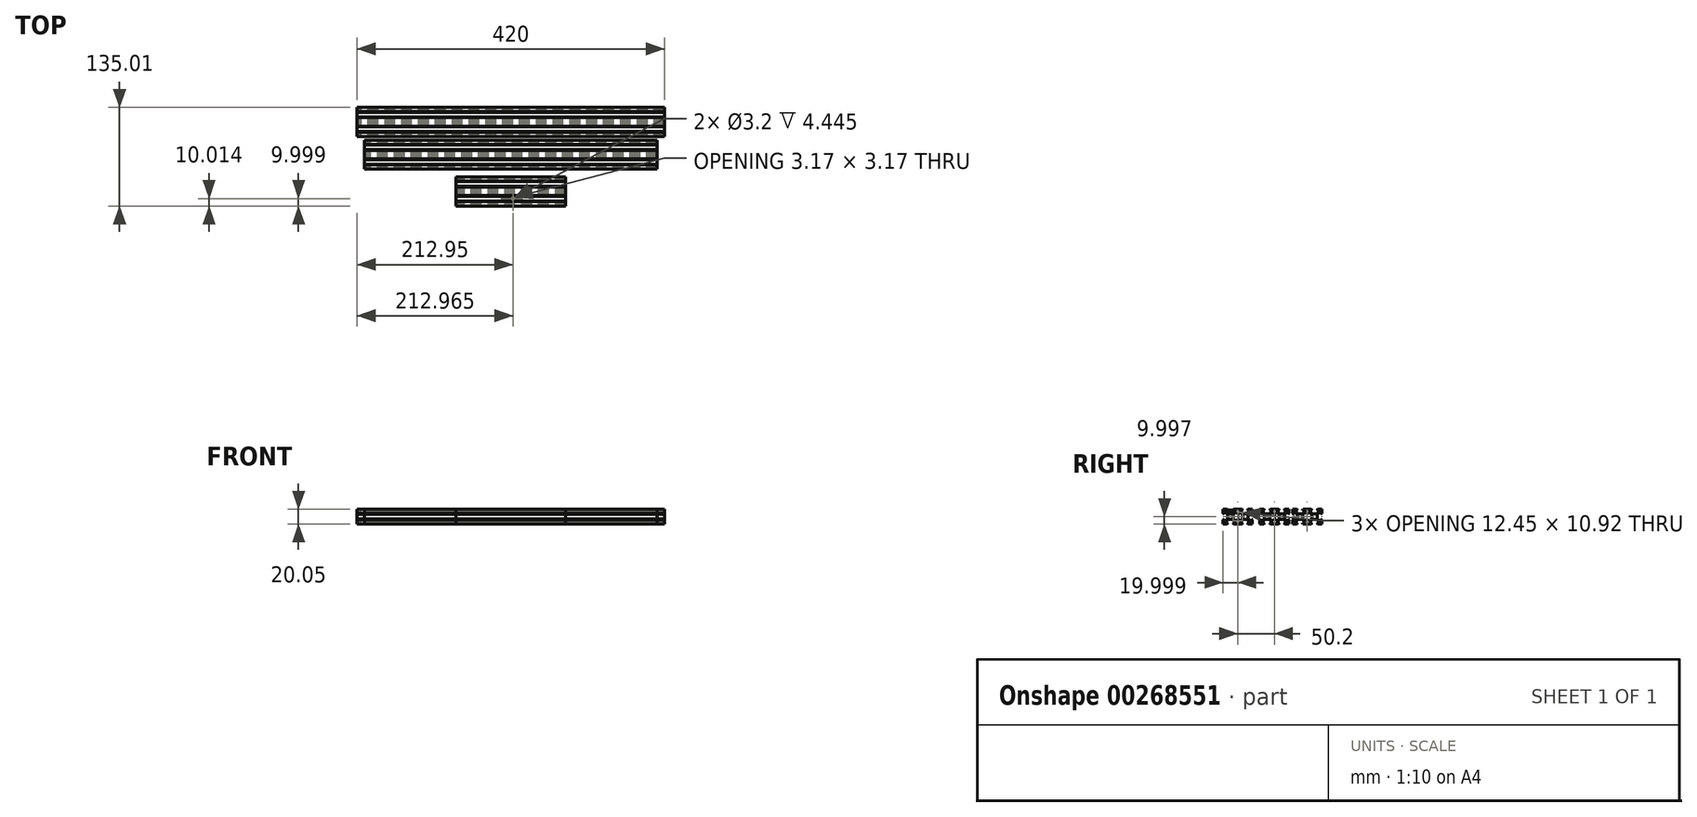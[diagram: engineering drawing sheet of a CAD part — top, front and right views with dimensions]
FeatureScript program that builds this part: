
annotation { "Feature Type Name" : "Feature", "Feature Type Description" : "" }
export const myFeature = defineFeature(function(context is Context, id is Id, definition is map)
    precondition{}
    {
        {
            var Q0;
            Q0=qCreatedBy(makeId("Right.planeOp"),FACE);
            var sketch = newSketch(context, id + "F0", { "sketchPlane" : qUnion([Q0])});
            skLineSegment(sketch, "E0.bottom", {"start": v(10.27, -9.71) * mm, "end": v(-9.73, -9.71) * mm});
            skLineSegment(sketch, "E0.top", {"start": v(10.27, 10.29) * mm, "end": v(-9.73, 10.29) * mm});
            skLineSegment(sketch, "E0.left", {"start": v(10.27, -9.71) * mm, "end": v(10.27, 10.29) * mm});
            skLineSegment(sketch, "E0.right", {"start": v(-9.73, -9.71) * mm, "end": v(-9.73, 10.29) * mm});
            skPoint(sketch, "E0.middle", {"position": v(0.27, 0.29) * mm});
            skLineSegment(sketch, "E1", {"start": v(4.51, 10.29) * mm, "end": v(3.38, 8.71) * mm});
            skLineSegment(sketch, "E2", {"start": v(3.38, 8.71) * mm, "end": v(3.38, 8.5) * mm});
            skLineSegment(sketch, "E3", {"start": v(3.38, 8.5) * mm, "end": v(5.73, 8.5) * mm});
            skLineSegment(sketch, "E4", {"start": v(5.73, 8.5) * mm, "end": v(5.73, 6.73) * mm});
            skLineSegment(sketch, "E5", {"start": v(5.73, 6.73) * mm, "end": v(3.38, 4.06) * mm});
            skLineSegment(sketch, "E6", {"start": v(3.38, 4.06) * mm, "end": v(0.27, 4.06) * mm});
            skLineSegment(sketch, "E7", {"start": v(0.27, 16.16) * mm, "end": v(0.27, -18.08) * mm, "construction": true});
            skPoint(sketch, "E7.endSnap0", {"position": v(0.27, -9.71) * mm});
            skLineSegment(sketch, "E8.0", {"start": v(5.73, 16.16) * mm, "end": v(5.73, -18.08) * mm, "construction": true});
            skLineSegment(sketch, "E9.MirrorCS", {"start": v(-3.98, 10.29) * mm, "end": v(-2.84, 8.71) * mm});
            skLineSegment(sketch, "E10.MirrorCS", {"start": v(-2.84, 8.71) * mm, "end": v(-2.84, 8.5) * mm});
            skLineSegment(sketch, "E11.MirrorCS", {"start": v(-2.84, 8.5) * mm, "end": v(-5.2, 8.5) * mm});
            skLineSegment(sketch, "E12.MirrorCS", {"start": v(-5.2, 16.16) * mm, "end": v(-5.2, -18.08) * mm, "construction": true});
            skLineSegment(sketch, "E13.MirrorCS", {"start": v(-5.2, 6.73) * mm, "end": v(-2.84, 4.06) * mm});
            skLineSegment(sketch, "E14.MirrorCS", {"start": v(-2.84, 4.06) * mm, "end": v(0.27, 4.06) * mm});
            skLineSegment(sketch, "E15.MirrorCS", {"start": v(-5.2, 8.5) * mm, "end": v(-5.2, 6.73) * mm});
            skLineSegment(sketch, "E16.1.0", {"start": v(-3.5, 3.4) * mm, "end": v(-3.5, 0.29) * mm});
            skLineSegment(sketch, "E16.1.1", {"start": v(-3.5, -2.82) * mm, "end": v(-3.5, 0.29) * mm});
            skLineSegment(sketch, "E16.1.2", {"start": v(-6.18, -5.17) * mm, "end": v(-3.5, -2.82) * mm});
            skLineSegment(sketch, "E16.1.3", {"start": v(-7.95, 3.4) * mm, "end": v(-7.95, 5.75) * mm});
            skLineSegment(sketch, "E16.1.4", {"start": v(-9.73, 4.53) * mm, "end": v(-8.16, 3.4) * mm});
            skLineSegment(sketch, "E16.1.5", {"start": v(-7.95, 5.75) * mm, "end": v(-6.18, 5.75) * mm});
            skLineSegment(sketch, "E16.1.6", {"start": v(-9.73, -3.96) * mm, "end": v(-8.16, -2.82) * mm});
            skLineSegment(sketch, "E16.1.7", {"start": v(-6.18, 5.75) * mm, "end": v(-3.5, 3.4) * mm});
            skLineSegment(sketch, "E16.1.8", {"start": v(-7.95, -5.17) * mm, "end": v(-6.18, -5.17) * mm});
            skLineSegment(sketch, "E16.1.9", {"start": v(-7.95, -2.82) * mm, "end": v(-7.95, -5.17) * mm});
            skLineSegment(sketch, "E16.1.10", {"start": v(-8.16, -2.82) * mm, "end": v(-7.95, -2.82) * mm});
            skLineSegment(sketch, "E16.1.11", {"start": v(-8.16, 3.4) * mm, "end": v(-7.95, 3.4) * mm});
            skLineSegment(sketch, "E16.2.0", {"start": v(-2.84, -3.5) * mm, "end": v(0.27, -3.5) * mm});
            skLineSegment(sketch, "E16.2.1", {"start": v(3.38, -3.5) * mm, "end": v(0.27, -3.5) * mm});
            skLineSegment(sketch, "E16.2.2", {"start": v(5.73, -6.16) * mm, "end": v(3.38, -3.5) * mm});
            skLineSegment(sketch, "E16.2.3", {"start": v(-2.84, -7.94) * mm, "end": v(-5.2, -7.94) * mm});
            skLineSegment(sketch, "E16.2.4", {"start": v(-3.98, -9.71) * mm, "end": v(-2.84, -8.14) * mm});
            skLineSegment(sketch, "E16.2.5", {"start": v(-5.2, -7.94) * mm, "end": v(-5.2, -6.16) * mm});
            skLineSegment(sketch, "E16.2.6", {"start": v(4.51, -9.71) * mm, "end": v(3.38, -8.14) * mm});
            skLineSegment(sketch, "E16.2.7", {"start": v(-5.2, -6.16) * mm, "end": v(-2.84, -3.5) * mm});
            skLineSegment(sketch, "E16.2.8", {"start": v(5.73, -7.94) * mm, "end": v(5.73, -6.16) * mm});
            skLineSegment(sketch, "E16.2.9", {"start": v(3.38, -7.94) * mm, "end": v(5.73, -7.94) * mm});
            skLineSegment(sketch, "E16.2.10", {"start": v(3.38, -8.14) * mm, "end": v(3.38, -7.94) * mm});
            skLineSegment(sketch, "E16.2.11", {"start": v(-2.84, -8.14) * mm, "end": v(-2.84, -7.94) * mm});
            skLineSegment(sketch, "E16.3.0", {"start": v(4.05, -2.82) * mm, "end": v(4.05, 0.29) * mm});
            skLineSegment(sketch, "E16.3.1", {"start": v(4.05, 3.4) * mm, "end": v(4.05, 0.29) * mm});
            skLineSegment(sketch, "E16.3.2", {"start": v(6.71, 5.75) * mm, "end": v(4.05, 3.4) * mm});
            skLineSegment(sketch, "E16.3.3", {"start": v(8.5, -2.82) * mm, "end": v(8.5, -5.17) * mm});
            skLineSegment(sketch, "E16.3.4", {"start": v(10.27, -3.96) * mm, "end": v(8.7, -2.82) * mm});
            skLineSegment(sketch, "E16.3.5", {"start": v(8.5, -5.17) * mm, "end": v(6.71, -5.17) * mm});
            skLineSegment(sketch, "E16.3.6", {"start": v(10.27, 4.53) * mm, "end": v(8.7, 3.4) * mm});
            skLineSegment(sketch, "E16.3.7", {"start": v(6.71, -5.17) * mm, "end": v(4.05, -2.82) * mm});
            skLineSegment(sketch, "E16.3.8", {"start": v(8.5, 5.75) * mm, "end": v(6.71, 5.75) * mm});
            skLineSegment(sketch, "E16.3.9", {"start": v(8.5, 3.4) * mm, "end": v(8.5, 5.75) * mm});
            skLineSegment(sketch, "E16.3.10", {"start": v(8.7, 3.4) * mm, "end": v(8.5, 3.4) * mm});
            skLineSegment(sketch, "E16.3.11", {"start": v(8.7, -2.82) * mm, "end": v(8.5, -2.82) * mm});
            skLineSegment(sketch, "E17.bottom", {"start": v(30.27, -9.71) * mm, "end": v(10.27, -9.71) * mm});
            skLineSegment(sketch, "E17.top", {"start": v(30.27, 10.29) * mm, "end": v(10.27, 10.29) * mm});
            skLineSegment(sketch, "E17.left", {"start": v(30.27, -9.71) * mm, "end": v(30.27, 10.29) * mm});
            skPoint(sketch, "E17.middle", {"position": v(20.27, 0.29) * mm});
            skLineSegment(sketch, "E18", {"start": v(24.51, 10.29) * mm, "end": v(23.38, 8.71) * mm});
            skLineSegment(sketch, "E19", {"start": v(23.38, 8.71) * mm, "end": v(23.38, 8.5) * mm});
            skLineSegment(sketch, "E20", {"start": v(23.38, 8.5) * mm, "end": v(25.73, 8.5) * mm});
            skLineSegment(sketch, "E21", {"start": v(25.73, 8.5) * mm, "end": v(25.73, 6.73) * mm});
            skLineSegment(sketch, "E22", {"start": v(25.73, 6.73) * mm, "end": v(23.38, 4.06) * mm});
            skLineSegment(sketch, "E23", {"start": v(23.38, 4.06) * mm, "end": v(20.27, 4.06) * mm});
            skPoint(sketch, "E24.endSnap0", {"position": v(20.27, -9.71) * mm});
            skLineSegment(sketch, "E25.MirrorCS", {"start": v(16.02, 10.29) * mm, "end": v(17.16, 8.71) * mm});
            skLineSegment(sketch, "E26.MirrorCS", {"start": v(17.16, 8.71) * mm, "end": v(17.16, 8.5) * mm});
            skLineSegment(sketch, "E27.MirrorCS", {"start": v(17.16, 8.5) * mm, "end": v(14.8, 8.5) * mm});
            skLineSegment(sketch, "E28.MirrorCS", {"start": v(14.8, 6.73) * mm, "end": v(17.16, 4.06) * mm});
            skLineSegment(sketch, "E29.MirrorCS", {"start": v(17.16, 4.06) * mm, "end": v(20.27, 4.06) * mm});
            skLineSegment(sketch, "E30.MirrorCS", {"start": v(14.8, 8.5) * mm, "end": v(14.8, 6.73) * mm});
            skLineSegment(sketch, "E31.1.0", {"start": v(16.5, 3.4) * mm, "end": v(16.5, 0.29) * mm});
            skLineSegment(sketch, "E31.1.1", {"start": v(16.5, -2.82) * mm, "end": v(16.5, 0.29) * mm});
            skLineSegment(sketch, "E31.1.2", {"start": v(13.82, -5.17) * mm, "end": v(16.5, -2.82) * mm});
            skLineSegment(sketch, "E31.1.3", {"start": v(12.05, 3.4) * mm, "end": v(12.05, 5.75) * mm});
            skLineSegment(sketch, "E31.1.4", {"start": v(10.27, 4.53) * mm, "end": v(11.84, 3.4) * mm});
            skLineSegment(sketch, "E31.1.5", {"start": v(12.05, 5.75) * mm, "end": v(13.82, 5.75) * mm});
            skLineSegment(sketch, "E31.1.6", {"start": v(10.27, -3.96) * mm, "end": v(11.84, -2.82) * mm});
            skLineSegment(sketch, "E31.1.7", {"start": v(13.82, 5.75) * mm, "end": v(16.5, 3.4) * mm});
            skLineSegment(sketch, "E31.1.8", {"start": v(12.05, -5.17) * mm, "end": v(13.82, -5.17) * mm});
            skLineSegment(sketch, "E31.1.9", {"start": v(12.05, -2.82) * mm, "end": v(12.05, -5.17) * mm});
            skLineSegment(sketch, "E31.1.10", {"start": v(11.84, -2.82) * mm, "end": v(12.05, -2.82) * mm});
            skLineSegment(sketch, "E31.1.11", {"start": v(11.84, 3.4) * mm, "end": v(12.05, 3.4) * mm});
            skLineSegment(sketch, "E31.2.0", {"start": v(17.16, -3.5) * mm, "end": v(20.27, -3.5) * mm});
            skLineSegment(sketch, "E31.2.1", {"start": v(23.38, -3.5) * mm, "end": v(20.27, -3.5) * mm});
            skLineSegment(sketch, "E31.2.2", {"start": v(25.73, -6.16) * mm, "end": v(23.38, -3.5) * mm});
            skLineSegment(sketch, "E31.2.3", {"start": v(17.16, -7.94) * mm, "end": v(14.8, -7.94) * mm});
            skLineSegment(sketch, "E31.2.4", {"start": v(16.02, -9.71) * mm, "end": v(17.16, -8.14) * mm});
            skLineSegment(sketch, "E31.2.5", {"start": v(14.8, -7.94) * mm, "end": v(14.8, -6.16) * mm});
            skLineSegment(sketch, "E31.2.6", {"start": v(24.51, -9.71) * mm, "end": v(23.38, -8.14) * mm});
            skLineSegment(sketch, "E31.2.7", {"start": v(14.8, -6.16) * mm, "end": v(17.16, -3.5) * mm});
            skLineSegment(sketch, "E31.2.8", {"start": v(25.73, -7.94) * mm, "end": v(25.73, -6.16) * mm});
            skLineSegment(sketch, "E31.2.9", {"start": v(23.38, -7.94) * mm, "end": v(25.73, -7.94) * mm});
            skLineSegment(sketch, "E31.2.10", {"start": v(23.38, -8.14) * mm, "end": v(23.38, -7.94) * mm});
            skLineSegment(sketch, "E31.2.11", {"start": v(17.16, -8.14) * mm, "end": v(17.16, -7.94) * mm});
            skLineSegment(sketch, "E31.3.0", {"start": v(24.05, -2.82) * mm, "end": v(24.05, 0.29) * mm});
            skLineSegment(sketch, "E31.3.1", {"start": v(24.05, 3.4) * mm, "end": v(24.05, 0.29) * mm});
            skLineSegment(sketch, "E31.3.2", {"start": v(26.71, 5.75) * mm, "end": v(24.05, 3.4) * mm});
            skLineSegment(sketch, "E31.3.3", {"start": v(28.5, -2.82) * mm, "end": v(28.5, -5.17) * mm});
            skLineSegment(sketch, "E31.3.4", {"start": v(30.27, -3.96) * mm, "end": v(28.7, -2.82) * mm});
            skLineSegment(sketch, "E31.3.5", {"start": v(28.5, -5.17) * mm, "end": v(26.71, -5.17) * mm});
            skLineSegment(sketch, "E31.3.6", {"start": v(30.27, 4.53) * mm, "end": v(28.7, 3.4) * mm});
            skLineSegment(sketch, "E31.3.7", {"start": v(26.71, -5.17) * mm, "end": v(24.05, -2.82) * mm});
            skLineSegment(sketch, "E31.3.8", {"start": v(28.5, 5.75) * mm, "end": v(26.71, 5.75) * mm});
            skLineSegment(sketch, "E31.3.9", {"start": v(28.5, 3.4) * mm, "end": v(28.5, 5.75) * mm});
            skLineSegment(sketch, "E31.3.10", {"start": v(28.7, 3.4) * mm, "end": v(28.5, 3.4) * mm});
            skLineSegment(sketch, "E31.3.11", {"start": v(28.7, -2.82) * mm, "end": v(28.5, -2.82) * mm});
            skSolve(sketch);
        }
        {
            var Q0;
            {var subQ11=sQuery(id+"F0.wireOp",EDGE,"E18");Q0=makeQuery(id+"F0.imprint","IMPRINT",FACE,{"disambiguationData":[TD([[makeQuery(id+"F0.imprint","IMPRINT",EDGE,{"derivedFrom":subQ11}),1.0]])]});}
            var Q1;
            {var subQ12=sQuery(id+"F0.wireOp",EDGE,"E1");Q1=makeQuery(id+"F0.imprint","IMPRINT",FACE,{"disambiguationData":[TD([[makeQuery(id+"F0.imprint","IMPRINT",EDGE,{"derivedFrom":subQ12}),1.0]])]});}
            extrude(context, id + "F1", {"entities" : qUnion([Q0, Q1]), "endBound" : BoundingType.SYMMETRIC, "depth" : 420 * mm});
        }
        {
            var Q0;
            Q0=qCreatedBy(makeId("Right.planeOp"),FACE);
            var sketch = newSketch(context, id + "F2", { "sketchPlane" : qUnion([Q0])});
            skLineSegment(sketch, "E32.bottom", {"start": v(0.66, -9.76) * mm, "end": v(-19.34, -9.76) * mm});
            skLineSegment(sketch, "E32.top", {"start": v(0.66, 10.24) * mm, "end": v(-19.34, 10.24) * mm});
            skLineSegment(sketch, "E32.left", {"start": v(0.66, -9.76) * mm, "end": v(0.66, 10.24) * mm});
            skLineSegment(sketch, "E32.right", {"start": v(-19.34, -9.76) * mm, "end": v(-19.34, 10.24) * mm});
            skPoint(sketch, "E32.middle", {"position": v(-9.34, 0.24) * mm});
            skLineSegment(sketch, "E33", {"start": v(-5.1, 10.24) * mm, "end": v(-6.23, 8.66) * mm});
            skLineSegment(sketch, "E34", {"start": v(-6.23, 8.66) * mm, "end": v(-6.23, 8.46) * mm});
            skLineSegment(sketch, "E35", {"start": v(-6.23, 8.46) * mm, "end": v(-3.88, 8.46) * mm});
            skLineSegment(sketch, "E36", {"start": v(-3.88, 8.46) * mm, "end": v(-3.88, 6.68) * mm});
            skLineSegment(sketch, "E37", {"start": v(-3.88, 6.68) * mm, "end": v(-6.23, 4.01) * mm});
            skLineSegment(sketch, "E38", {"start": v(-6.23, 4.01) * mm, "end": v(-9.34, 4.01) * mm});
            skLineSegment(sketch, "E39", {"start": v(-9.34, 16.11) * mm, "end": v(-9.34, -18.13) * mm, "construction": true});
            skPoint(sketch, "E39.endSnap0", {"position": v(-9.34, -9.76) * mm});
            skLineSegment(sketch, "E40.0", {"start": v(-3.88, 16.11) * mm, "end": v(-3.88, -18.13) * mm, "construction": true});
            skLineSegment(sketch, "E41.MirrorCS", {"start": v(-13.59, 10.24) * mm, "end": v(-12.45, 8.66) * mm});
            skLineSegment(sketch, "E42.MirrorCS", {"start": v(-12.45, 8.66) * mm, "end": v(-12.45, 8.46) * mm});
            skLineSegment(sketch, "E43.MirrorCS", {"start": v(-12.45, 8.46) * mm, "end": v(-14.8, 8.46) * mm});
            skLineSegment(sketch, "E44.MirrorCS", {"start": v(-14.8, 16.11) * mm, "end": v(-14.8, -18.13) * mm, "construction": true});
            skLineSegment(sketch, "E45.MirrorCS", {"start": v(-14.8, 6.68) * mm, "end": v(-12.45, 4.01) * mm});
            skLineSegment(sketch, "E46.MirrorCS", {"start": v(-12.45, 4.01) * mm, "end": v(-9.34, 4.01) * mm});
            skLineSegment(sketch, "E47.MirrorCS", {"start": v(-14.8, 8.46) * mm, "end": v(-14.8, 6.68) * mm});
            skLineSegment(sketch, "E48.1.0", {"start": v(-13.12, 3.35) * mm, "end": v(-13.12, 0.24) * mm});
            skLineSegment(sketch, "E48.1.1", {"start": v(-13.12, -2.87) * mm, "end": v(-13.12, 0.24) * mm});
            skLineSegment(sketch, "E48.1.2", {"start": v(-15.79, -5.22) * mm, "end": v(-13.12, -2.87) * mm});
            skLineSegment(sketch, "E48.1.3", {"start": v(-17.56, 3.35) * mm, "end": v(-17.56, 5.7) * mm});
            skLineSegment(sketch, "E48.1.4", {"start": v(-19.34, 4.48) * mm, "end": v(-17.77, 3.35) * mm});
            skLineSegment(sketch, "E48.1.5", {"start": v(-17.56, 5.7) * mm, "end": v(-15.79, 5.7) * mm});
            skLineSegment(sketch, "E48.1.6", {"start": v(-19.34, -4) * mm, "end": v(-17.77, -2.87) * mm});
            skLineSegment(sketch, "E48.1.7", {"start": v(-15.79, 5.7) * mm, "end": v(-13.12, 3.35) * mm});
            skLineSegment(sketch, "E48.1.8", {"start": v(-17.56, -5.22) * mm, "end": v(-15.79, -5.22) * mm});
            skLineSegment(sketch, "E48.1.9", {"start": v(-17.56, -2.87) * mm, "end": v(-17.56, -5.22) * mm});
            skLineSegment(sketch, "E48.1.10", {"start": v(-17.77, -2.87) * mm, "end": v(-17.56, -2.87) * mm});
            skLineSegment(sketch, "E48.1.11", {"start": v(-17.77, 3.35) * mm, "end": v(-17.56, 3.35) * mm});
            skLineSegment(sketch, "E48.2.0", {"start": v(-12.45, -3.54) * mm, "end": v(-9.34, -3.54) * mm});
            skLineSegment(sketch, "E48.2.1", {"start": v(-6.23, -3.54) * mm, "end": v(-9.34, -3.54) * mm});
            skLineSegment(sketch, "E48.2.2", {"start": v(-3.88, -6.2) * mm, "end": v(-6.23, -3.54) * mm});
            skLineSegment(sketch, "E48.2.3", {"start": v(-12.45, -7.98) * mm, "end": v(-14.8, -7.98) * mm});
            skLineSegment(sketch, "E48.2.4", {"start": v(-13.59, -9.76) * mm, "end": v(-12.45, -8.19) * mm});
            skLineSegment(sketch, "E48.2.5", {"start": v(-14.8, -7.98) * mm, "end": v(-14.8, -6.2) * mm});
            skLineSegment(sketch, "E48.2.6", {"start": v(-5.1, -9.76) * mm, "end": v(-6.23, -8.19) * mm});
            skLineSegment(sketch, "E48.2.7", {"start": v(-14.8, -6.2) * mm, "end": v(-12.45, -3.54) * mm});
            skLineSegment(sketch, "E48.2.8", {"start": v(-3.88, -7.98) * mm, "end": v(-3.88, -6.2) * mm});
            skLineSegment(sketch, "E48.2.9", {"start": v(-6.23, -7.98) * mm, "end": v(-3.88, -7.98) * mm});
            skLineSegment(sketch, "E48.2.10", {"start": v(-6.23, -8.19) * mm, "end": v(-6.23, -7.98) * mm});
            skLineSegment(sketch, "E48.2.11", {"start": v(-12.45, -8.19) * mm, "end": v(-12.45, -7.98) * mm});
            skLineSegment(sketch, "E48.3.0", {"start": v(-5.56, -2.87) * mm, "end": v(-5.56, 0.24) * mm});
            skLineSegment(sketch, "E48.3.1", {"start": v(-5.56, 3.35) * mm, "end": v(-5.56, 0.24) * mm});
            skLineSegment(sketch, "E48.3.2", {"start": v(-2.9, 5.7) * mm, "end": v(-5.56, 3.35) * mm});
            skLineSegment(sketch, "E48.3.3", {"start": v(-1.12, -2.87) * mm, "end": v(-1.12, -5.22) * mm});
            skLineSegment(sketch, "E48.3.4", {"start": v(0.66, -4) * mm, "end": v(-0.92, -2.87) * mm});
            skLineSegment(sketch, "E48.3.5", {"start": v(-1.12, -5.22) * mm, "end": v(-2.9, -5.22) * mm});
            skLineSegment(sketch, "E48.3.6", {"start": v(0.66, 4.48) * mm, "end": v(-0.92, 3.35) * mm});
            skLineSegment(sketch, "E48.3.7", {"start": v(-2.9, -5.22) * mm, "end": v(-5.56, -2.87) * mm});
            skLineSegment(sketch, "E48.3.8", {"start": v(-1.12, 5.7) * mm, "end": v(-2.9, 5.7) * mm});
            skLineSegment(sketch, "E48.3.9", {"start": v(-1.12, 3.35) * mm, "end": v(-1.12, 5.7) * mm});
            skLineSegment(sketch, "E48.3.10", {"start": v(-0.92, 3.35) * mm, "end": v(-1.12, 3.35) * mm});
            skLineSegment(sketch, "E48.3.11", {"start": v(-0.92, -2.87) * mm, "end": v(-1.12, -2.87) * mm});
            skLineSegment(sketch, "E49.bottom", {"start": v(20.66, -9.76) * mm, "end": v(0.66, -9.76) * mm});
            skLineSegment(sketch, "E49.top", {"start": v(20.66, 10.24) * mm, "end": v(0.66, 10.24) * mm});
            skLineSegment(sketch, "E49.left", {"start": v(20.66, -9.76) * mm, "end": v(20.66, 10.24) * mm});
            skPoint(sketch, "E49.middle", {"position": v(10.66, 0.24) * mm});
            skLineSegment(sketch, "E50", {"start": v(14.9, 10.24) * mm, "end": v(13.77, 8.66) * mm});
            skLineSegment(sketch, "E51", {"start": v(13.77, 8.66) * mm, "end": v(13.77, 8.46) * mm});
            skLineSegment(sketch, "E52", {"start": v(13.77, 8.46) * mm, "end": v(16.12, 8.46) * mm});
            skLineSegment(sketch, "E53", {"start": v(16.12, 8.46) * mm, "end": v(16.12, 6.68) * mm});
            skLineSegment(sketch, "E54", {"start": v(16.12, 6.68) * mm, "end": v(13.77, 4.01) * mm});
            skLineSegment(sketch, "E55", {"start": v(13.77, 4.01) * mm, "end": v(10.66, 4.01) * mm});
            skPoint(sketch, "E56.endSnap0", {"position": v(10.66, -9.76) * mm});
            skLineSegment(sketch, "E57.MirrorCS", {"start": v(6.41, 10.24) * mm, "end": v(7.55, 8.66) * mm});
            skLineSegment(sketch, "E58.MirrorCS", {"start": v(7.55, 8.66) * mm, "end": v(7.55, 8.46) * mm});
            skLineSegment(sketch, "E59.MirrorCS", {"start": v(7.55, 8.46) * mm, "end": v(5.2, 8.46) * mm});
            skLineSegment(sketch, "E60.MirrorCS", {"start": v(5.2, 6.68) * mm, "end": v(7.55, 4.01) * mm});
            skLineSegment(sketch, "E61.MirrorCS", {"start": v(7.55, 4.01) * mm, "end": v(10.66, 4.01) * mm});
            skLineSegment(sketch, "E62.MirrorCS", {"start": v(5.2, 8.46) * mm, "end": v(5.2, 6.68) * mm});
            skLineSegment(sketch, "E63.1.0", {"start": v(6.88, 3.35) * mm, "end": v(6.88, 0.24) * mm});
            skLineSegment(sketch, "E63.1.1", {"start": v(6.88, -2.87) * mm, "end": v(6.88, 0.24) * mm});
            skLineSegment(sketch, "E63.1.2", {"start": v(4.21, -5.22) * mm, "end": v(6.88, -2.87) * mm});
            skLineSegment(sketch, "E63.1.3", {"start": v(2.44, 3.35) * mm, "end": v(2.44, 5.7) * mm});
            skLineSegment(sketch, "E63.1.4", {"start": v(0.66, 4.48) * mm, "end": v(2.23, 3.35) * mm});
            skLineSegment(sketch, "E63.1.5", {"start": v(2.44, 5.7) * mm, "end": v(4.21, 5.7) * mm});
            skLineSegment(sketch, "E63.1.6", {"start": v(0.66, -4) * mm, "end": v(2.23, -2.87) * mm});
            skLineSegment(sketch, "E63.1.7", {"start": v(4.21, 5.7) * mm, "end": v(6.88, 3.35) * mm});
            skLineSegment(sketch, "E63.1.8", {"start": v(2.44, -5.22) * mm, "end": v(4.21, -5.22) * mm});
            skLineSegment(sketch, "E63.1.9", {"start": v(2.44, -2.87) * mm, "end": v(2.44, -5.22) * mm});
            skLineSegment(sketch, "E63.1.10", {"start": v(2.23, -2.87) * mm, "end": v(2.44, -2.87) * mm});
            skLineSegment(sketch, "E63.1.11", {"start": v(2.23, 3.35) * mm, "end": v(2.44, 3.35) * mm});
            skLineSegment(sketch, "E63.2.0", {"start": v(7.55, -3.54) * mm, "end": v(10.66, -3.54) * mm});
            skLineSegment(sketch, "E63.2.1", {"start": v(13.77, -3.54) * mm, "end": v(10.66, -3.54) * mm});
            skLineSegment(sketch, "E63.2.2", {"start": v(16.12, -6.2) * mm, "end": v(13.77, -3.54) * mm});
            skLineSegment(sketch, "E63.2.3", {"start": v(7.55, -7.98) * mm, "end": v(5.2, -7.98) * mm});
            skLineSegment(sketch, "E63.2.4", {"start": v(6.41, -9.76) * mm, "end": v(7.55, -8.19) * mm});
            skLineSegment(sketch, "E63.2.5", {"start": v(5.2, -7.98) * mm, "end": v(5.2, -6.2) * mm});
            skLineSegment(sketch, "E63.2.6", {"start": v(14.9, -9.76) * mm, "end": v(13.77, -8.19) * mm});
            skLineSegment(sketch, "E63.2.7", {"start": v(5.2, -6.2) * mm, "end": v(7.55, -3.54) * mm});
            skLineSegment(sketch, "E63.2.8", {"start": v(16.12, -7.98) * mm, "end": v(16.12, -6.2) * mm});
            skLineSegment(sketch, "E63.2.9", {"start": v(13.77, -7.98) * mm, "end": v(16.12, -7.98) * mm});
            skLineSegment(sketch, "E63.2.10", {"start": v(13.77, -8.19) * mm, "end": v(13.77, -7.98) * mm});
            skLineSegment(sketch, "E63.2.11", {"start": v(7.55, -8.19) * mm, "end": v(7.55, -7.98) * mm});
            skLineSegment(sketch, "E63.3.0", {"start": v(14.44, -2.87) * mm, "end": v(14.44, 0.24) * mm});
            skLineSegment(sketch, "E63.3.1", {"start": v(14.44, 3.35) * mm, "end": v(14.44, 0.24) * mm});
            skLineSegment(sketch, "E63.3.2", {"start": v(17.1, 5.7) * mm, "end": v(14.44, 3.35) * mm});
            skLineSegment(sketch, "E63.3.3", {"start": v(18.88, -2.87) * mm, "end": v(18.88, -5.22) * mm});
            skLineSegment(sketch, "E63.3.4", {"start": v(20.66, -4) * mm, "end": v(19.08, -2.87) * mm});
            skLineSegment(sketch, "E63.3.5", {"start": v(18.88, -5.22) * mm, "end": v(17.1, -5.22) * mm});
            skLineSegment(sketch, "E63.3.6", {"start": v(20.66, 4.48) * mm, "end": v(19.08, 3.35) * mm});
            skLineSegment(sketch, "E63.3.7", {"start": v(17.1, -5.22) * mm, "end": v(14.44, -2.87) * mm});
            skLineSegment(sketch, "E63.3.8", {"start": v(18.88, 5.7) * mm, "end": v(17.1, 5.7) * mm});
            skLineSegment(sketch, "E63.3.9", {"start": v(18.88, 3.35) * mm, "end": v(18.88, 5.7) * mm});
            skLineSegment(sketch, "E63.3.10", {"start": v(19.08, 3.35) * mm, "end": v(18.88, 3.35) * mm});
            skLineSegment(sketch, "E63.3.11", {"start": v(19.08, -2.87) * mm, "end": v(18.88, -2.87) * mm});
            skSolve(sketch);
        }
        {
            var Q0;
            Q0=makeQuery(id+"F1.opExtrude","SWEPT_BODY",BODY,{"disambiguationData":[OSD([sQuery(id+"F0.wireOp",EDGE,"E0.bottom"),sQuery(id+"F0.wireOp",EDGE,"E0.top"),sQuery(id+"F0.wireOp",EDGE,"E0.right"),sQuery(id+"F0.wireOp",EDGE,"E1"),sQuery(id+"F0.wireOp",EDGE,"E2"),sQuery(id+"F0.wireOp",EDGE,"E3"),sQuery(id+"F0.wireOp",EDGE,"E4"),sQuery(id+"F0.wireOp",EDGE,"E5"),sQuery(id+"F0.wireOp",EDGE,"E6"),sQuery(id+"F0.wireOp",EDGE,"E9.MirrorCS"),sQuery(id+"F0.wireOp",EDGE,"E10.MirrorCS"),sQuery(id+"F0.wireOp",EDGE,"E11.MirrorCS"),sQuery(id+"F0.wireOp",EDGE,"E13.MirrorCS"),sQuery(id+"F0.wireOp",EDGE,"E14.MirrorCS"),sQuery(id+"F0.wireOp",EDGE,"E15.MirrorCS"),sQuery(id+"F0.wireOp",EDGE,"E16.1.0"),sQuery(id+"F0.wireOp",EDGE,"E16.1.1"),sQuery(id+"F0.wireOp",EDGE,"E16.1.2"),sQuery(id+"F0.wireOp",EDGE,"E16.1.3"),sQuery(id+"F0.wireOp",EDGE,"E16.1.4"),sQuery(id+"F0.wireOp",EDGE,"E16.1.5"),sQuery(id+"F0.wireOp",EDGE,"E16.1.6"),sQuery(id+"F0.wireOp",EDGE,"E16.1.7"),sQuery(id+"F0.wireOp",EDGE,"E16.1.8"),sQuery(id+"F0.wireOp",EDGE,"E16.1.9"),sQuery(id+"F0.wireOp",EDGE,"E16.1.10"),sQuery(id+"F0.wireOp",EDGE,"E16.1.11"),sQuery(id+"F0.wireOp",EDGE,"E16.2.0"),sQuery(id+"F0.wireOp",EDGE,"E16.2.1"),sQuery(id+"F0.wireOp",EDGE,"E16.2.2"),sQuery(id+"F0.wireOp",EDGE,"E16.2.3"),sQuery(id+"F0.wireOp",EDGE,"E16.2.4"),sQuery(id+"F0.wireOp",EDGE,"E16.2.5"),sQuery(id+"F0.wireOp",EDGE,"E16.2.6"),sQuery(id+"F0.wireOp",EDGE,"E16.2.7"),sQuery(id+"F0.wireOp",EDGE,"E16.2.8"),sQuery(id+"F0.wireOp",EDGE,"E16.2.9"),sQuery(id+"F0.wireOp",EDGE,"E16.2.10"),sQuery(id+"F0.wireOp",EDGE,"E16.2.11"),sQuery(id+"F0.wireOp",EDGE,"E16.3.0"),sQuery(id+"F0.wireOp",EDGE,"E16.3.1"),sQuery(id+"F0.wireOp",EDGE,"E16.3.2"),sQuery(id+"F0.wireOp",EDGE,"E16.3.3"),sQuery(id+"F0.wireOp",EDGE,"E16.3.4"),sQuery(id+"F0.wireOp",EDGE,"E16.3.5"),sQuery(id+"F0.wireOp",EDGE,"E16.3.6"),sQuery(id+"F0.wireOp",EDGE,"E16.3.7"),sQuery(id+"F0.wireOp",EDGE,"E16.3.8"),sQuery(id+"F0.wireOp",EDGE,"E16.3.9"),sQuery(id+"F0.wireOp",EDGE,"E16.3.10"),sQuery(id+"F0.wireOp",EDGE,"E16.3.11"),sQuery(id+"F0.wireOp",EDGE,"E17.bottom"),sQuery(id+"F0.wireOp",EDGE,"E17.top"),sQuery(id+"F0.wireOp",EDGE,"E17.left"),sQuery(id+"F0.wireOp",EDGE,"E18"),sQuery(id+"F0.wireOp",EDGE,"E19"),sQuery(id+"F0.wireOp",EDGE,"E20"),sQuery(id+"F0.wireOp",EDGE,"E21"),sQuery(id+"F0.wireOp",EDGE,"E22"),sQuery(id+"F0.wireOp",EDGE,"E23"),sQuery(id+"F0.wireOp",EDGE,"E25.MirrorCS"),sQuery(id+"F0.wireOp",EDGE,"E26.MirrorCS"),sQuery(id+"F0.wireOp",EDGE,"E27.MirrorCS"),sQuery(id+"F0.wireOp",EDGE,"E28.MirrorCS"),sQuery(id+"F0.wireOp",EDGE,"E29.MirrorCS"),sQuery(id+"F0.wireOp",EDGE,"E30.MirrorCS"),sQuery(id+"F0.wireOp",EDGE,"E31.1.0"),sQuery(id+"F0.wireOp",EDGE,"E31.1.1"),sQuery(id+"F0.wireOp",EDGE,"E31.1.2"),sQuery(id+"F0.wireOp",EDGE,"E31.1.3"),sQuery(id+"F0.wireOp",EDGE,"E31.1.4"),sQuery(id+"F0.wireOp",EDGE,"E31.1.5"),sQuery(id+"F0.wireOp",EDGE,"E31.1.6"),sQuery(id+"F0.wireOp",EDGE,"E31.1.7"),sQuery(id+"F0.wireOp",EDGE,"E31.1.8"),sQuery(id+"F0.wireOp",EDGE,"E31.1.9"),sQuery(id+"F0.wireOp",EDGE,"E31.1.10"),sQuery(id+"F0.wireOp",EDGE,"E31.1.11"),sQuery(id+"F0.wireOp",EDGE,"E31.2.0"),sQuery(id+"F0.wireOp",EDGE,"E31.2.1"),sQuery(id+"F0.wireOp",EDGE,"E31.2.2"),sQuery(id+"F0.wireOp",EDGE,"E31.2.3"),sQuery(id+"F0.wireOp",EDGE,"E31.2.4"),sQuery(id+"F0.wireOp",EDGE,"E31.2.5"),sQuery(id+"F0.wireOp",EDGE,"E31.2.6"),sQuery(id+"F0.wireOp",EDGE,"E31.2.7"),sQuery(id+"F0.wireOp",EDGE,"E31.2.8"),sQuery(id+"F0.wireOp",EDGE,"E31.2.9"),sQuery(id+"F0.wireOp",EDGE,"E31.2.10"),sQuery(id+"F0.wireOp",EDGE,"E31.2.11"),sQuery(id+"F0.wireOp",EDGE,"E31.3.0"),sQuery(id+"F0.wireOp",EDGE,"E31.3.1"),sQuery(id+"F0.wireOp",EDGE,"E31.3.2"),sQuery(id+"F0.wireOp",EDGE,"E31.3.3"),sQuery(id+"F0.wireOp",EDGE,"E31.3.4"),sQuery(id+"F0.wireOp",EDGE,"E31.3.5"),sQuery(id+"F0.wireOp",EDGE,"E31.3.6"),sQuery(id+"F0.wireOp",EDGE,"E31.3.7"),sQuery(id+"F0.wireOp",EDGE,"E31.3.8"),sQuery(id+"F0.wireOp",EDGE,"E31.3.9"),sQuery(id+"F0.wireOp",EDGE,"E31.3.10"),sQuery(id+"F0.wireOp",EDGE,"E31.3.11")])]});
            transform(context, id + "F3", {"entities" : qUnion([Q0]), "transformType" : TransformType.TRANSLATION_3D, "dx" : 0 * mm, "dy" : 35.2 * mm, "dz" : 0 * mm, "makeCopy" : false});
        }
        {
            var Q0;
            {var subQ12=sQuery(id+"F2.wireOp",EDGE,"E33");Q0=makeQuery(id+"F2.imprint","IMPRINT",FACE,{"disambiguationData":[TD([[makeQuery(id+"F2.imprint","IMPRINT",EDGE,{"derivedFrom":subQ12}),1.0]])]});}
            var Q1;
            {var subQ4=sQuery(id+"F2.wireOp",EDGE,"E50");Q1=makeQuery(id+"F2.imprint","IMPRINT",FACE,{"disambiguationData":[TD([[makeQuery(id+"F2.imprint","IMPRINT",EDGE,{"derivedFrom":subQ4}),1.0]])]});}
            extrude(context, id + "F4", {"entities" : qUnion([Q0, Q1]), "endBound" : BoundingType.SYMMETRIC, "depth" : 150 * mm});
        }
        {
            var Q0;
            Q0=makeQuery(id+"F4.opExtrude","SWEPT_BODY",BODY,{"disambiguationData":[OSD([sQuery(id+"F2.wireOp",EDGE,"E32.bottom"),sQuery(id+"F2.wireOp",EDGE,"E32.top"),sQuery(id+"F2.wireOp",EDGE,"E32.right"),sQuery(id+"F2.wireOp",EDGE,"E33"),sQuery(id+"F2.wireOp",EDGE,"E34"),sQuery(id+"F2.wireOp",EDGE,"E35"),sQuery(id+"F2.wireOp",EDGE,"E36"),sQuery(id+"F2.wireOp",EDGE,"E37"),sQuery(id+"F2.wireOp",EDGE,"E38"),sQuery(id+"F2.wireOp",EDGE,"E41.MirrorCS"),sQuery(id+"F2.wireOp",EDGE,"E42.MirrorCS"),sQuery(id+"F2.wireOp",EDGE,"E43.MirrorCS"),sQuery(id+"F2.wireOp",EDGE,"E45.MirrorCS"),sQuery(id+"F2.wireOp",EDGE,"E46.MirrorCS"),sQuery(id+"F2.wireOp",EDGE,"E47.MirrorCS"),sQuery(id+"F2.wireOp",EDGE,"E48.1.0"),sQuery(id+"F2.wireOp",EDGE,"E48.1.1"),sQuery(id+"F2.wireOp",EDGE,"E48.1.2"),sQuery(id+"F2.wireOp",EDGE,"E48.1.3"),sQuery(id+"F2.wireOp",EDGE,"E48.1.4"),sQuery(id+"F2.wireOp",EDGE,"E48.1.5"),sQuery(id+"F2.wireOp",EDGE,"E48.1.6"),sQuery(id+"F2.wireOp",EDGE,"E48.1.7"),sQuery(id+"F2.wireOp",EDGE,"E48.1.8"),sQuery(id+"F2.wireOp",EDGE,"E48.1.9"),sQuery(id+"F2.wireOp",EDGE,"E48.1.10"),sQuery(id+"F2.wireOp",EDGE,"E48.1.11"),sQuery(id+"F2.wireOp",EDGE,"E48.2.0"),sQuery(id+"F2.wireOp",EDGE,"E48.2.1"),sQuery(id+"F2.wireOp",EDGE,"E48.2.2"),sQuery(id+"F2.wireOp",EDGE,"E48.2.3"),sQuery(id+"F2.wireOp",EDGE,"E48.2.4"),sQuery(id+"F2.wireOp",EDGE,"E48.2.5"),sQuery(id+"F2.wireOp",EDGE,"E48.2.6"),sQuery(id+"F2.wireOp",EDGE,"E48.2.7"),sQuery(id+"F2.wireOp",EDGE,"E48.2.8"),sQuery(id+"F2.wireOp",EDGE,"E48.2.9"),sQuery(id+"F2.wireOp",EDGE,"E48.2.10"),sQuery(id+"F2.wireOp",EDGE,"E48.2.11"),sQuery(id+"F2.wireOp",EDGE,"E48.3.0"),sQuery(id+"F2.wireOp",EDGE,"E48.3.1"),sQuery(id+"F2.wireOp",EDGE,"E48.3.2"),sQuery(id+"F2.wireOp",EDGE,"E48.3.3"),sQuery(id+"F2.wireOp",EDGE,"E48.3.4"),sQuery(id+"F2.wireOp",EDGE,"E48.3.5"),sQuery(id+"F2.wireOp",EDGE,"E48.3.6"),sQuery(id+"F2.wireOp",EDGE,"E48.3.7"),sQuery(id+"F2.wireOp",EDGE,"E48.3.8"),sQuery(id+"F2.wireOp",EDGE,"E48.3.9"),sQuery(id+"F2.wireOp",EDGE,"E48.3.10"),sQuery(id+"F2.wireOp",EDGE,"E48.3.11"),sQuery(id+"F2.wireOp",EDGE,"E49.bottom"),sQuery(id+"F2.wireOp",EDGE,"E49.top"),sQuery(id+"F2.wireOp",EDGE,"E49.left"),sQuery(id+"F2.wireOp",EDGE,"E50"),sQuery(id+"F2.wireOp",EDGE,"E51"),sQuery(id+"F2.wireOp",EDGE,"E52"),sQuery(id+"F2.wireOp",EDGE,"E53"),sQuery(id+"F2.wireOp",EDGE,"E54"),sQuery(id+"F2.wireOp",EDGE,"E55"),sQuery(id+"F2.wireOp",EDGE,"E57.MirrorCS"),sQuery(id+"F2.wireOp",EDGE,"E58.MirrorCS"),sQuery(id+"F2.wireOp",EDGE,"E59.MirrorCS"),sQuery(id+"F2.wireOp",EDGE,"E60.MirrorCS"),sQuery(id+"F2.wireOp",EDGE,"E61.MirrorCS"),sQuery(id+"F2.wireOp",EDGE,"E62.MirrorCS"),sQuery(id+"F2.wireOp",EDGE,"E63.1.0"),sQuery(id+"F2.wireOp",EDGE,"E63.1.1"),sQuery(id+"F2.wireOp",EDGE,"E63.1.2"),sQuery(id+"F2.wireOp",EDGE,"E63.1.3"),sQuery(id+"F2.wireOp",EDGE,"E63.1.4"),sQuery(id+"F2.wireOp",EDGE,"E63.1.5"),sQuery(id+"F2.wireOp",EDGE,"E63.1.6"),sQuery(id+"F2.wireOp",EDGE,"E63.1.7"),sQuery(id+"F2.wireOp",EDGE,"E63.1.8"),sQuery(id+"F2.wireOp",EDGE,"E63.1.9"),sQuery(id+"F2.wireOp",EDGE,"E63.1.10"),sQuery(id+"F2.wireOp",EDGE,"E63.1.11"),sQuery(id+"F2.wireOp",EDGE,"E63.2.0"),sQuery(id+"F2.wireOp",EDGE,"E63.2.1"),sQuery(id+"F2.wireOp",EDGE,"E63.2.2"),sQuery(id+"F2.wireOp",EDGE,"E63.2.3"),sQuery(id+"F2.wireOp",EDGE,"E63.2.4"),sQuery(id+"F2.wireOp",EDGE,"E63.2.5"),sQuery(id+"F2.wireOp",EDGE,"E63.2.6"),sQuery(id+"F2.wireOp",EDGE,"E63.2.7"),sQuery(id+"F2.wireOp",EDGE,"E63.2.8"),sQuery(id+"F2.wireOp",EDGE,"E63.2.9"),sQuery(id+"F2.wireOp",EDGE,"E63.2.10"),sQuery(id+"F2.wireOp",EDGE,"E63.2.11"),sQuery(id+"F2.wireOp",EDGE,"E63.3.0"),sQuery(id+"F2.wireOp",EDGE,"E63.3.1"),sQuery(id+"F2.wireOp",EDGE,"E63.3.2"),sQuery(id+"F2.wireOp",EDGE,"E63.3.3"),sQuery(id+"F2.wireOp",EDGE,"E63.3.4"),sQuery(id+"F2.wireOp",EDGE,"E63.3.5"),sQuery(id+"F2.wireOp",EDGE,"E63.3.6"),sQuery(id+"F2.wireOp",EDGE,"E63.3.7"),sQuery(id+"F2.wireOp",EDGE,"E63.3.8"),sQuery(id+"F2.wireOp",EDGE,"E63.3.9"),sQuery(id+"F2.wireOp",EDGE,"E63.3.10"),sQuery(id+"F2.wireOp",EDGE,"E63.3.11")])]});
            transform(context, id + "F5", {"entities" : qUnion([Q0]), "transformType" : TransformType.TRANSLATION_3D, "dx" : 0 * mm, "dy" : -50.2 * mm, "dz" : 0 * mm, "makeCopy" : false});
        }
        {
            var Q0;
            Q0=qCreatedBy(makeId("Right.planeOp"),FACE);
            var sketch = newSketch(context, id + "F6", { "sketchPlane" : qUnion([Q0])});
            skLineSegment(sketch, "E64.bottom", {"start": v(0.66, -9.76) * mm, "end": v(-19.34, -9.76) * mm});
            skLineSegment(sketch, "E64.top", {"start": v(0.66, 10.24) * mm, "end": v(-19.34, 10.24) * mm});
            skLineSegment(sketch, "E64.left", {"start": v(0.66, -9.76) * mm, "end": v(0.66, 10.24) * mm});
            skLineSegment(sketch, "E64.right", {"start": v(-19.34, -9.76) * mm, "end": v(-19.34, 10.24) * mm});
            skPoint(sketch, "E64.middle", {"position": v(-9.34, 0.24) * mm});
            skLineSegment(sketch, "E65", {"start": v(-5.1, 10.24) * mm, "end": v(-6.23, 8.66) * mm});
            skLineSegment(sketch, "E66", {"start": v(-6.23, 8.66) * mm, "end": v(-6.23, 8.46) * mm});
            skLineSegment(sketch, "E67", {"start": v(-6.23, 8.46) * mm, "end": v(-3.88, 8.46) * mm});
            skLineSegment(sketch, "E68", {"start": v(-3.88, 8.46) * mm, "end": v(-3.88, 6.68) * mm});
            skLineSegment(sketch, "E69", {"start": v(-3.88, 6.68) * mm, "end": v(-6.23, 4.01) * mm});
            skLineSegment(sketch, "E70", {"start": v(-6.23, 4.01) * mm, "end": v(-9.34, 4.01) * mm});
            skLineSegment(sketch, "E71", {"start": v(-9.34, 16.11) * mm, "end": v(-9.34, -18.13) * mm, "construction": true});
            skPoint(sketch, "E71.endSnap0", {"position": v(-9.34, -9.76) * mm});
            skLineSegment(sketch, "E72.0", {"start": v(-3.88, 16.11) * mm, "end": v(-3.88, -18.13) * mm, "construction": true});
            skLineSegment(sketch, "E73.MirrorCS", {"start": v(-13.59, 10.24) * mm, "end": v(-12.45, 8.66) * mm});
            skLineSegment(sketch, "E74.MirrorCS", {"start": v(-12.45, 8.66) * mm, "end": v(-12.45, 8.46) * mm});
            skLineSegment(sketch, "E75.MirrorCS", {"start": v(-12.45, 8.46) * mm, "end": v(-14.8, 8.46) * mm});
            skLineSegment(sketch, "E76.MirrorCS", {"start": v(-14.8, 16.11) * mm, "end": v(-14.8, -18.13) * mm, "construction": true});
            skLineSegment(sketch, "E77.MirrorCS", {"start": v(-14.8, 6.68) * mm, "end": v(-12.45, 4.01) * mm});
            skLineSegment(sketch, "E78.MirrorCS", {"start": v(-12.45, 4.01) * mm, "end": v(-9.34, 4.01) * mm});
            skLineSegment(sketch, "E79.MirrorCS", {"start": v(-14.8, 8.46) * mm, "end": v(-14.8, 6.68) * mm});
            skLineSegment(sketch, "E80.1.0", {"start": v(-13.12, 3.35) * mm, "end": v(-13.12, 0.24) * mm});
            skLineSegment(sketch, "E80.1.1", {"start": v(-13.12, -2.87) * mm, "end": v(-13.12, 0.24) * mm});
            skLineSegment(sketch, "E80.1.2", {"start": v(-15.79, -5.22) * mm, "end": v(-13.12, -2.87) * mm});
            skLineSegment(sketch, "E80.1.3", {"start": v(-17.56, 3.35) * mm, "end": v(-17.56, 5.7) * mm});
            skLineSegment(sketch, "E80.1.4", {"start": v(-19.34, 4.48) * mm, "end": v(-17.77, 3.35) * mm});
            skLineSegment(sketch, "E80.1.5", {"start": v(-17.56, 5.7) * mm, "end": v(-15.79, 5.7) * mm});
            skLineSegment(sketch, "E80.1.6", {"start": v(-19.34, -4) * mm, "end": v(-17.77, -2.87) * mm});
            skLineSegment(sketch, "E80.1.7", {"start": v(-15.79, 5.7) * mm, "end": v(-13.12, 3.35) * mm});
            skLineSegment(sketch, "E80.1.8", {"start": v(-17.56, -5.22) * mm, "end": v(-15.79, -5.22) * mm});
            skLineSegment(sketch, "E80.1.9", {"start": v(-17.56, -2.87) * mm, "end": v(-17.56, -5.22) * mm});
            skLineSegment(sketch, "E80.1.10", {"start": v(-17.77, -2.87) * mm, "end": v(-17.56, -2.87) * mm});
            skLineSegment(sketch, "E80.1.11", {"start": v(-17.77, 3.35) * mm, "end": v(-17.56, 3.35) * mm});
            skLineSegment(sketch, "E80.2.0", {"start": v(-12.45, -3.54) * mm, "end": v(-9.34, -3.54) * mm});
            skLineSegment(sketch, "E80.2.1", {"start": v(-6.23, -3.54) * mm, "end": v(-9.34, -3.54) * mm});
            skLineSegment(sketch, "E80.2.2", {"start": v(-3.88, -6.2) * mm, "end": v(-6.23, -3.54) * mm});
            skLineSegment(sketch, "E80.2.3", {"start": v(-12.45, -7.98) * mm, "end": v(-14.8, -7.98) * mm});
            skLineSegment(sketch, "E80.2.4", {"start": v(-13.59, -9.76) * mm, "end": v(-12.45, -8.19) * mm});
            skLineSegment(sketch, "E80.2.5", {"start": v(-14.8, -7.98) * mm, "end": v(-14.8, -6.2) * mm});
            skLineSegment(sketch, "E80.2.6", {"start": v(-5.1, -9.76) * mm, "end": v(-6.23, -8.19) * mm});
            skLineSegment(sketch, "E80.2.7", {"start": v(-14.8, -6.2) * mm, "end": v(-12.45, -3.54) * mm});
            skLineSegment(sketch, "E80.2.8", {"start": v(-3.88, -7.98) * mm, "end": v(-3.88, -6.2) * mm});
            skLineSegment(sketch, "E80.2.9", {"start": v(-6.23, -7.98) * mm, "end": v(-3.88, -7.98) * mm});
            skLineSegment(sketch, "E80.2.10", {"start": v(-6.23, -8.19) * mm, "end": v(-6.23, -7.98) * mm});
            skLineSegment(sketch, "E80.2.11", {"start": v(-12.45, -8.19) * mm, "end": v(-12.45, -7.98) * mm});
            skLineSegment(sketch, "E80.3.0", {"start": v(-5.56, -2.87) * mm, "end": v(-5.56, 0.24) * mm});
            skLineSegment(sketch, "E80.3.1", {"start": v(-5.56, 3.35) * mm, "end": v(-5.56, 0.24) * mm});
            skLineSegment(sketch, "E80.3.2", {"start": v(-2.9, 5.7) * mm, "end": v(-5.56, 3.35) * mm});
            skLineSegment(sketch, "E80.3.3", {"start": v(-1.12, -2.87) * mm, "end": v(-1.12, -5.22) * mm});
            skLineSegment(sketch, "E80.3.4", {"start": v(0.66, -4) * mm, "end": v(-0.92, -2.87) * mm});
            skLineSegment(sketch, "E80.3.5", {"start": v(-1.12, -5.22) * mm, "end": v(-2.9, -5.22) * mm});
            skLineSegment(sketch, "E80.3.6", {"start": v(0.66, 4.48) * mm, "end": v(-0.92, 3.35) * mm});
            skLineSegment(sketch, "E80.3.7", {"start": v(-2.9, -5.22) * mm, "end": v(-5.56, -2.87) * mm});
            skLineSegment(sketch, "E80.3.8", {"start": v(-1.12, 5.7) * mm, "end": v(-2.9, 5.7) * mm});
            skLineSegment(sketch, "E80.3.9", {"start": v(-1.12, 3.35) * mm, "end": v(-1.12, 5.7) * mm});
            skLineSegment(sketch, "E80.3.10", {"start": v(-0.92, 3.35) * mm, "end": v(-1.12, 3.35) * mm});
            skLineSegment(sketch, "E80.3.11", {"start": v(-0.92, -2.87) * mm, "end": v(-1.12, -2.87) * mm});
            skLineSegment(sketch, "E81.bottom", {"start": v(20.66, -9.76) * mm, "end": v(0.66, -9.76) * mm});
            skLineSegment(sketch, "E81.top", {"start": v(20.66, 10.24) * mm, "end": v(0.66, 10.24) * mm});
            skLineSegment(sketch, "E81.left", {"start": v(20.66, -9.76) * mm, "end": v(20.66, 10.24) * mm});
            skPoint(sketch, "E81.middle", {"position": v(10.66, 0.24) * mm});
            skLineSegment(sketch, "E82", {"start": v(14.9, 10.24) * mm, "end": v(13.77, 8.66) * mm});
            skLineSegment(sketch, "E83", {"start": v(13.77, 8.66) * mm, "end": v(13.77, 8.46) * mm});
            skLineSegment(sketch, "E84", {"start": v(13.77, 8.46) * mm, "end": v(16.12, 8.46) * mm});
            skLineSegment(sketch, "E85", {"start": v(16.12, 8.46) * mm, "end": v(16.12, 6.68) * mm});
            skLineSegment(sketch, "E86", {"start": v(16.12, 6.68) * mm, "end": v(13.77, 4.01) * mm});
            skLineSegment(sketch, "E87", {"start": v(13.77, 4.01) * mm, "end": v(10.66, 4.01) * mm});
            skPoint(sketch, "E88.endSnap0", {"position": v(10.66, -9.76) * mm});
            skLineSegment(sketch, "E89.MirrorCS", {"start": v(6.41, 10.24) * mm, "end": v(7.55, 8.66) * mm});
            skLineSegment(sketch, "E90.MirrorCS", {"start": v(7.55, 8.66) * mm, "end": v(7.55, 8.46) * mm});
            skLineSegment(sketch, "E91.MirrorCS", {"start": v(7.55, 8.46) * mm, "end": v(5.2, 8.46) * mm});
            skLineSegment(sketch, "E92.MirrorCS", {"start": v(5.2, 6.68) * mm, "end": v(7.55, 4.01) * mm});
            skLineSegment(sketch, "E93.MirrorCS", {"start": v(7.55, 4.01) * mm, "end": v(10.66, 4.01) * mm});
            skLineSegment(sketch, "E94.MirrorCS", {"start": v(5.2, 8.46) * mm, "end": v(5.2, 6.68) * mm});
            skLineSegment(sketch, "E95.1.0", {"start": v(6.88, 3.35) * mm, "end": v(6.88, 0.24) * mm});
            skLineSegment(sketch, "E95.1.1", {"start": v(6.88, -2.87) * mm, "end": v(6.88, 0.24) * mm});
            skLineSegment(sketch, "E95.1.2", {"start": v(4.21, -5.22) * mm, "end": v(6.88, -2.87) * mm});
            skLineSegment(sketch, "E95.1.3", {"start": v(2.44, 3.35) * mm, "end": v(2.44, 5.7) * mm});
            skLineSegment(sketch, "E95.1.4", {"start": v(0.66, 4.48) * mm, "end": v(2.23, 3.35) * mm});
            skLineSegment(sketch, "E95.1.5", {"start": v(2.44, 5.7) * mm, "end": v(4.21, 5.7) * mm});
            skLineSegment(sketch, "E95.1.6", {"start": v(0.66, -4) * mm, "end": v(2.23, -2.87) * mm});
            skLineSegment(sketch, "E95.1.7", {"start": v(4.21, 5.7) * mm, "end": v(6.88, 3.35) * mm});
            skLineSegment(sketch, "E95.1.8", {"start": v(2.44, -5.22) * mm, "end": v(4.21, -5.22) * mm});
            skLineSegment(sketch, "E95.1.9", {"start": v(2.44, -2.87) * mm, "end": v(2.44, -5.22) * mm});
            skLineSegment(sketch, "E95.1.10", {"start": v(2.23, -2.87) * mm, "end": v(2.44, -2.87) * mm});
            skLineSegment(sketch, "E95.1.11", {"start": v(2.23, 3.35) * mm, "end": v(2.44, 3.35) * mm});
            skLineSegment(sketch, "E95.2.0", {"start": v(7.55, -3.54) * mm, "end": v(10.66, -3.54) * mm});
            skLineSegment(sketch, "E95.2.1", {"start": v(13.77, -3.54) * mm, "end": v(10.66, -3.54) * mm});
            skLineSegment(sketch, "E95.2.2", {"start": v(16.12, -6.2) * mm, "end": v(13.77, -3.54) * mm});
            skLineSegment(sketch, "E95.2.3", {"start": v(7.55, -7.98) * mm, "end": v(5.2, -7.98) * mm});
            skLineSegment(sketch, "E95.2.4", {"start": v(6.41, -9.76) * mm, "end": v(7.55, -8.19) * mm});
            skLineSegment(sketch, "E95.2.5", {"start": v(5.2, -7.98) * mm, "end": v(5.2, -6.2) * mm});
            skLineSegment(sketch, "E95.2.6", {"start": v(14.9, -9.76) * mm, "end": v(13.77, -8.19) * mm});
            skLineSegment(sketch, "E95.2.7", {"start": v(5.2, -6.2) * mm, "end": v(7.55, -3.54) * mm});
            skLineSegment(sketch, "E95.2.8", {"start": v(16.12, -7.98) * mm, "end": v(16.12, -6.2) * mm});
            skLineSegment(sketch, "E95.2.9", {"start": v(13.77, -7.98) * mm, "end": v(16.12, -7.98) * mm});
            skLineSegment(sketch, "E95.2.10", {"start": v(13.77, -8.19) * mm, "end": v(13.77, -7.98) * mm});
            skLineSegment(sketch, "E95.2.11", {"start": v(7.55, -8.19) * mm, "end": v(7.55, -7.98) * mm});
            skLineSegment(sketch, "E95.3.0", {"start": v(14.44, -2.87) * mm, "end": v(14.44, 0.24) * mm});
            skLineSegment(sketch, "E95.3.1", {"start": v(14.44, 3.35) * mm, "end": v(14.44, 0.24) * mm});
            skLineSegment(sketch, "E95.3.2", {"start": v(17.1, 5.7) * mm, "end": v(14.44, 3.35) * mm});
            skLineSegment(sketch, "E95.3.3", {"start": v(18.88, -2.87) * mm, "end": v(18.88, -5.22) * mm});
            skLineSegment(sketch, "E95.3.4", {"start": v(20.66, -4) * mm, "end": v(19.08, -2.87) * mm});
            skLineSegment(sketch, "E95.3.5", {"start": v(18.88, -5.22) * mm, "end": v(17.1, -5.22) * mm});
            skLineSegment(sketch, "E95.3.6", {"start": v(20.66, 4.48) * mm, "end": v(19.08, 3.35) * mm});
            skLineSegment(sketch, "E95.3.7", {"start": v(17.1, -5.22) * mm, "end": v(14.44, -2.87) * mm});
            skLineSegment(sketch, "E95.3.8", {"start": v(18.88, 5.7) * mm, "end": v(17.1, 5.7) * mm});
            skLineSegment(sketch, "E95.3.9", {"start": v(18.88, 3.35) * mm, "end": v(18.88, 5.7) * mm});
            skLineSegment(sketch, "E95.3.10", {"start": v(19.08, 3.35) * mm, "end": v(18.88, 3.35) * mm});
            skLineSegment(sketch, "E95.3.11", {"start": v(19.08, -2.87) * mm, "end": v(18.88, -2.87) * mm});
            skSolve(sketch);
        }
        {
            var Q0;
            {var subQ3=sQuery(id+"F6.wireOp",EDGE,"E65");Q0=makeQuery(id+"F6.imprint","IMPRINT",FACE,{"disambiguationData":[TD([[makeQuery(id+"F6.imprint","IMPRINT",EDGE,{"derivedFrom":subQ3}),1.0]])]});}
            var Q1;
            {var subQ4=sQuery(id+"F6.wireOp",EDGE,"E82");Q1=makeQuery(id+"F6.imprint","IMPRINT",FACE,{"disambiguationData":[TD([[makeQuery(id+"F6.imprint","IMPRINT",EDGE,{"derivedFrom":subQ4}),1.0]])]});}
            extrude(context, id + "F7", {"entities" : qUnion([Q0, Q1]), "endBound" : BoundingType.SYMMETRIC, "depth" : 400 * mm});
        }
        {
            var Q0;
            Q0=qCreatedBy(makeId("Right.planeOp"),FACE);
            var sketch = newSketch(context, id + "F8", { "sketchPlane" : qUnion([Q0])});
            skLineSegment(sketch, "E96.0", {"start": v(-56.93, 7.96) * mm, "end": v(-56.93, 7.96) * mm});
            skLineSegment(sketch, "E96.1", {"start": v(-56.93, 7.96) * mm, "end": v(-54.58, 7.96) * mm});
            skLineSegment(sketch, "E96.2", {"start": v(-54.58, 7.96) * mm, "end": v(-54.58, 6.87) * mm});
            skLineSegment(sketch, "E96.3", {"start": v(-54.58, 6.87) * mm, "end": v(-56.66, 4.51) * mm});
            skLineSegment(sketch, "E96.4", {"start": v(-56.66, 4.51) * mm, "end": v(-62.43, 4.51) * mm});
            skLineSegment(sketch, "E96.5", {"start": v(-62.15, 7.96) * mm, "end": v(-62.15, 7.96) * mm});
            skLineSegment(sketch, "E96.6", {"start": v(-62.15, 7.96) * mm, "end": v(-64.5, 7.96) * mm});
            skLineSegment(sketch, "E96.7", {"start": v(-64.5, 7.96) * mm, "end": v(-64.5, 6.87) * mm});
            skLineSegment(sketch, "E96.8", {"start": v(-64.5, 6.87) * mm, "end": v(-62.43, 4.51) * mm});
            skLineSegment(sketch, "E97", {"start": v(-62.15, 7.96) * mm, "end": v(-56.93, 7.96) * mm});
            skSolve(sketch);
        }
        {
            var Q0;
            Q0=makeQuery(id+"F8.imprint","IMPRINT",FACE,{"disambiguationData":[TD([[makeQuery(id+"F8.imprint","IMPRINT",EDGE,{"derivedFrom":sQuery(id+"F8.wireOp",EDGE,"E96.1")}),-1.0]])]});
            extrude(context, id + "F9", {"entities" : qUnion([Q0]), "depth" : 5.9 * mm});
        }
        {
            var Q0;
            Q0=makeQuery(id+"F9.opExtrude","SWEPT_FACE",FACE,{"disambiguationData":[OSD([sQuery(id+"F8.wireOp",EDGE,"E96.1"),sQuery(id+"F8.wireOp",EDGE,"E96.6"),sQuery(id+"F8.wireOp",EDGE,"E97")])]});
            var sketch = newSketch(context, id + "F10", { "sketchPlane" : qUnion([Q0])});
            skCircle(sketch, "E98", {"center": v(2.95, -59.54) * mm, "radius": 2.5 * mm});
            skLineSegment(sketch, "E99", {"start": v(0, -64.5) * mm, "end": v(5.9, -54.58) * mm, "construction": true});
            skSolve(sketch);
        }
        {
            var Q0;
            Q0=makeQuery(id+"F10.imprint","IMPRINT",FACE,{"disambiguationData":[TD([[makeQuery(id+"F10.imprint","IMPRINT",EDGE,{"derivedFrom":sQuery(id+"F10.wireOp",EDGE,"E98")}),1.0]])]});
            extrude(context, id + "F11", {"entities" : qUnion([Q0]), "operationType" : NewBodyOperationType.ADD, "depth" : 1 * mm});
        }
        {
            var Q0;
            Q0=makeQuery(id+"F11.opExtrude","CAP_FACE",FACE,{"disambiguationData":[OSD([sQuery(id+"F10.wireOp",EDGE,"E98")])],"isStart":false});
            var sketch = newSketch(context, id + "F12", { "sketchPlane" : qUnion([Q0])});
            skCircle(sketch, "E100", {"center": v(2.95, -59.54) * mm, "radius": 1.6 * mm});
            skSolve(sketch);
        }
        {
            var Q0;
            Q0=makeQuery(id+"F12.imprint","IMPRINT",FACE,{"disambiguationData":[TD([[makeQuery(id+"F12.imprint","IMPRINT",EDGE,{"derivedFrom":sQuery(id+"F12.wireOp",EDGE,"E100")}),1.0]])]});
            extrude(context, id + "F13", {"entities" : qUnion([Q0]), "operationType" : NewBodyOperationType.REMOVE, "endBound" : BoundingType.UP_TO_NEXT, "oppositeDirection" : true, "depth" : 25 * mm});
        }
        {
            var Q0;
            Q0=makeQuery(id+"F9.opExtrude","SWEPT_BODY",BODY,{"disambiguationData":[OSD([sQuery(id+"F8.wireOp",EDGE,"E96.1"),sQuery(id+"F8.wireOp",EDGE,"E96.2"),sQuery(id+"F8.wireOp",EDGE,"E96.3"),sQuery(id+"F8.wireOp",EDGE,"E96.4"),sQuery(id+"F8.wireOp",EDGE,"E96.6"),sQuery(id+"F8.wireOp",EDGE,"E96.7"),sQuery(id+"F8.wireOp",EDGE,"E96.8"),sQuery(id+"F8.wireOp",EDGE,"E97")])]});
            transform(context, id + "F14", {"entities" : qUnion([Q0]), "transformType" : TransformType.TRANSLATION_3D, "dx" : 0 * mm, "dy" : 0 * mm, "dz" : 0 * mm, "makeCopy" : true});
        }
    });
